# Revit family: Sanitary_Taps-Mixers_TOTO-USA-Inc_LibellaT-M-EcoPower-Faucet-0-5-GPM
name_source: partatom
category: Plumbing Fixtures
revit_build: Autodesk Revit 2015 (Build: 20140606_1530(x64)
units: mm (PartAtom-declared; Revit-internal decimal feet)

## types (1)
- TELS1B5
    Ambient Temp. = 32-104°F(0-40°C)
    BIMobject category = Taps & Mixers
    BIMobject category code = sanitary-taps-mixers
    BIMobject main category = Sanitary
    BIMobject main category code = sanitary
    Brand url = https://www.totousa.com
    Default Elevation = 4' - 0"
    Description = EcoPower Faucet SPOUT ASSY LIBELLA M (0.5/Q)
    Edition number = 1
    Humidity = Max. 90% RH
    IFC Classification = Sanitary Terminal
    Installation instructions = https://www.totousa.com
    Manufacturer = TOTO
    Manufacturer name = TOTO USA Inc
    Masterformat 2014 Code = 10 28 00
    Masterformat 2014 Description = Toilet, Bath, and Laundry Accessories
    Material Main = Metal - TOTO - Steel
    Material Spout = Metal - TOTO - Polished Steel
    Model = TELS1B5
    NBS Reference Code = 35-06-07
    NBS Reference Description = Bath Water Supply Fittings
    OmniClass Code = 23-31 11 00
    OmniClass Description = Faucets
    Product Guid = 4cb8e91b-8983-47a5-8f0d-f6c6773842bc
    Product SKU = toto-tel1b5-d10e
    Product certification = https://www.totousa.com
    Product data url = https://bimobject.com
    Product family = Mixing Faucets
    Product group = Libella™
    Product name = Libella™ M EcoPower Faucet - 0.5 GPM
    Product url = https://www.totousa.com
    QR code = http://bimobject.com
    Sensor Detection Range = 5-1/8inch - 7-7/8inch (130 - 200mm)
    Technical description = https://www.totousa.com
    UNSPSC Code = 30181505
    Uniclass 1.4 Code = L725111
    Uniclass 1.4 Description = Mixer taps
    Uniclass 2.0 Code = PR-35-06-07
    Uniclass 2.0 Description = Bath Water Supply Fittings
    Uniclass 2015 Code = Pr_40_20_87_84
    Uniclass 2015 Name = Sink taps
    Uniformat II Code = D2030
    Uniformat II Description = Sanitary Waste
    Warranty = Three year limited
    Water Supply Pressure(Max) = 80.00 psi
    Water Supply Pressure(Min) = 15.00 psi

## geometry (parser evidence)
native form markers: Sweep x3
no freeform markers — native parametric forms only
